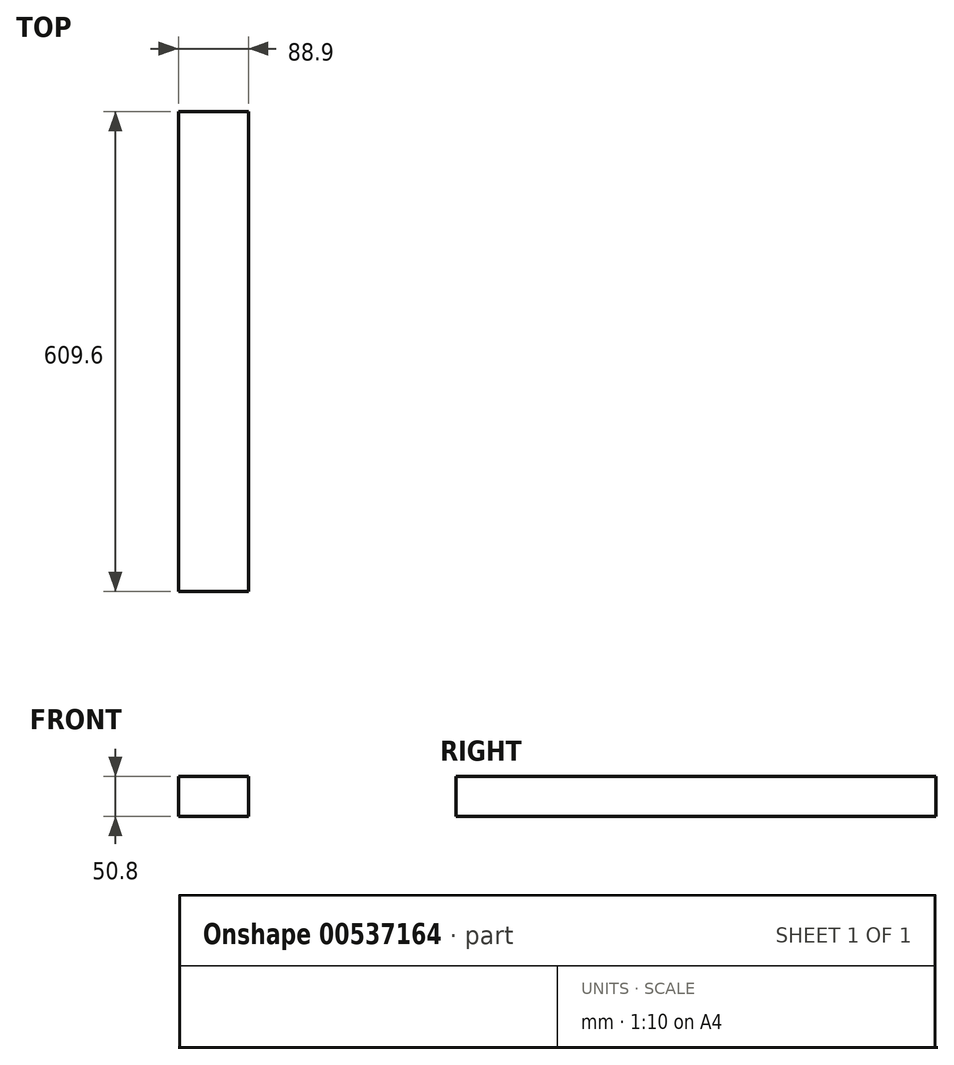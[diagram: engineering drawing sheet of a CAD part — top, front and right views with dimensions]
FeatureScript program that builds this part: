
annotation { "Feature Type Name" : "Feature", "Feature Type Description" : "" }
export const myFeature = defineFeature(function(context is Context, id is Id, definition is map)
    precondition{}
    {
        {
            var Q0;
            Q0=qCreatedBy(makeId("Front.planeOp"),FACE);
            var sketch = newSketch(context, id + "F0", { "sketchPlane" : qUnion([Q0])});
            skLineSegment(sketch, "E0.bottom", {"start": v(-59.42, 20.84) * mm, "end": v(29.48, 20.84) * mm});
            skLineSegment(sketch, "E0.top", {"start": v(-59.42, -29.96) * mm, "end": v(29.48, -29.96) * mm});
            skLineSegment(sketch, "E0.left", {"start": v(-59.42, 20.84) * mm, "end": v(-59.42, -29.96) * mm});
            skLineSegment(sketch, "E0.right", {"start": v(29.48, 20.84) * mm, "end": v(29.48, -29.96) * mm});
            skSolve(sketch);
        }
        {
            var Q0;
            Q0 = qSketchRegion(id + "F0", true);
            extrude(context, id + "F1", {"entities" : qUnion([Q0]), "depth" : 609.6 * mm, "offsetDistance" : 25.4 * mm});
        }
    });
